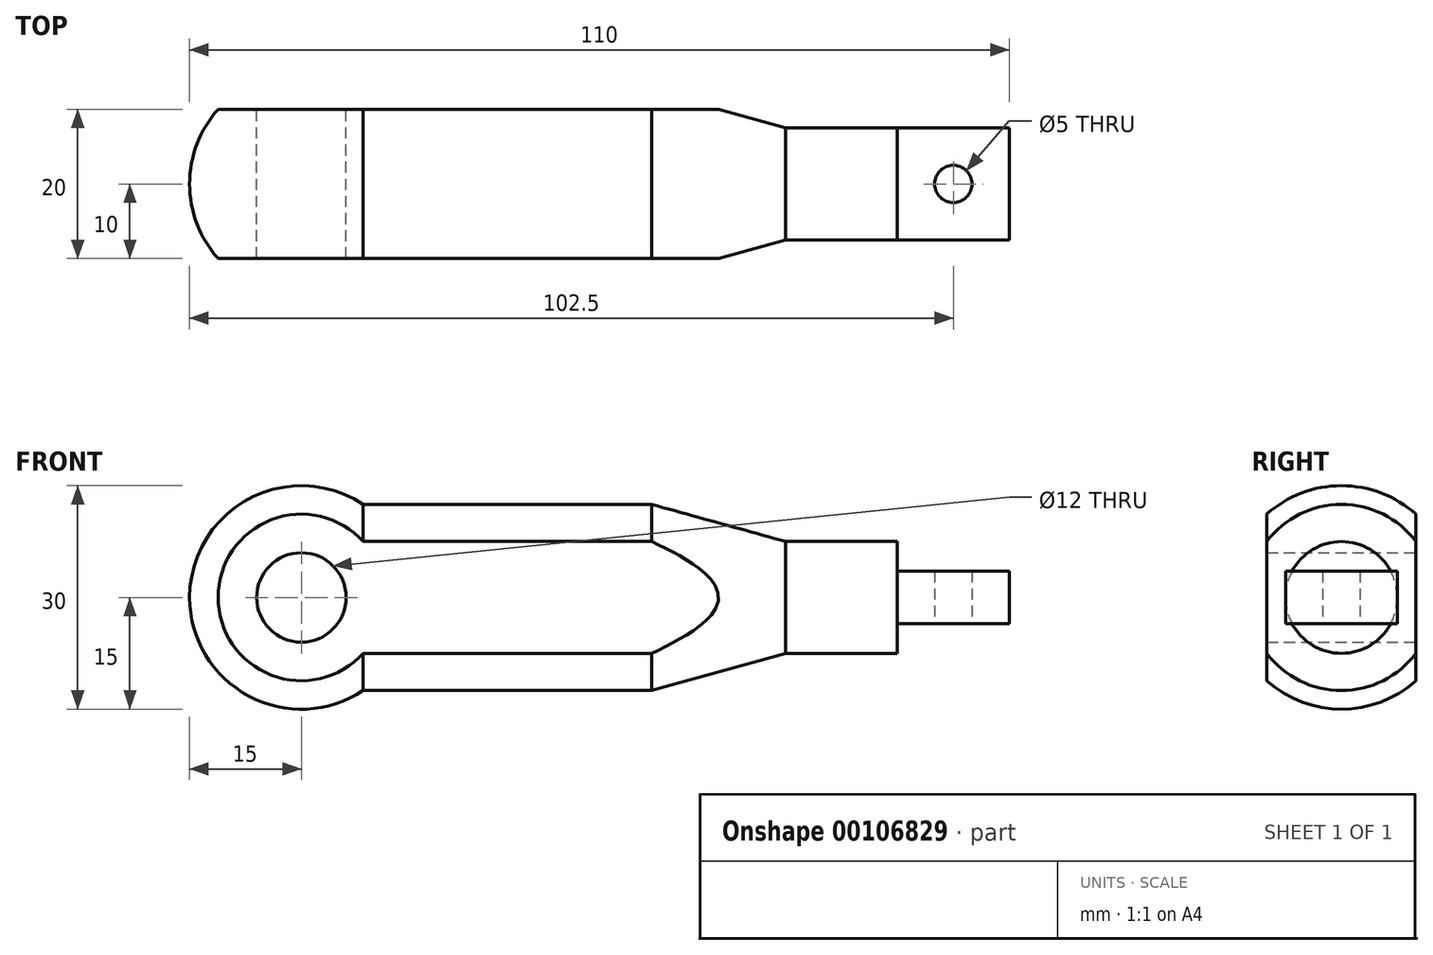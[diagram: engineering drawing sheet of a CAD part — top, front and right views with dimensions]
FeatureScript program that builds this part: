
annotation { "Feature Type Name" : "Feature", "Feature Type Description" : "" }
export const myFeature = defineFeature(function(context is Context, id is Id, definition is map)
    precondition{}
    {
        {
            var Q0;
            Q0=qCreatedBy(makeId("Front.planeOp"),FACE);
            var sketch = newSketch(context, id + "F0", { "sketchPlane" : qUnion([Q0])});
            skCircle(sketch, "E0", {"center": v(0, 0) * mm, "radius": 6 * mm});
            skLineSegment(sketch, "E1", {"start": v(0, 0) * mm, "end": v(135.17, 0) * mm, "construction": true});
            skLineSegment(sketch, "E2.bottom", {"start": v(80, 3.5) * mm, "end": v(95, 3.5) * mm});
            skLineSegment(sketch, "E2.top", {"start": v(80, -3.5) * mm, "end": v(95, -3.5) * mm});
            skLineSegment(sketch, "E2.left", {"start": v(80, 3.5) * mm, "end": v(80, -3.5) * mm});
            skLineSegment(sketch, "E2.right", {"start": v(95, 3.5) * mm, "end": v(95, -3.5) * mm});
            skSolve(sketch);
        }
        {
            var Q0;
            Q0=makeQuery(id+"F0.imprint","IMPRINT",FACE,{"disambiguationData":[TD([[makeQuery(id+"F0.imprint","IMPRINT",EDGE,{"derivedFrom":sQuery(id+"F0.wireOp",EDGE,"E2.bottom")}),-1.0]])]});
            extrude(context, id + "F1", {"entities" : qUnion([Q0]), "endBound" : BoundingType.SYMMETRIC, "depth" : 15 * mm});
        }
        {
            var Q0;
            Q0=qCreatedBy(makeId("Top.planeOp"),FACE);
            var sketch = newSketch(context, id + "F2", { "sketchPlane" : qUnion([Q0])});
            skLineSegment(sketch, "E3", {"start": v(-1.5, 0) * mm, "end": v(118.55, 0) * mm, "construction": true});
            skCircle(sketch, "E4", {"center": v(87.5, 0) * mm, "radius": 2.5 * mm});
            skSolve(sketch);
        }
        {
            var Q0;
            Q0=qCreatedBy(makeId("Front.planeOp"),FACE);
            var sketch = newSketch(context, id + "F3", { "sketchPlane" : qUnion([Q0])});
            skLineSegment(sketch, "E5.bottom", {"start": v(65, 7.5) * mm, "end": v(80, 7.5) * mm});
            skLineSegment(sketch, "E5.top", {"start": v(65, 0) * mm, "end": v(80, 0) * mm});
            skLineSegment(sketch, "E5.left", {"start": v(65, 7.5) * mm, "end": v(65, 0) * mm});
            skLineSegment(sketch, "E5.right", {"start": v(80, 7.5) * mm, "end": v(80, 0) * mm});
            skSolve(sketch);
        }
        {
            var Q0;
            Q0=makeQuery(id+"F3.imprint","IMPRINT",FACE,{"disambiguationData":[TD([[makeQuery(id+"F3.imprint","IMPRINT",EDGE,{"derivedFrom":sQuery(id+"F3.wireOp",EDGE,"E5.bottom")}),-1.0]])]});
            var Q1;
            Q1=sQuery(id+"F2.wireOp",EDGE,"E3");
            revolve(context, id + "F4", {"operationType" : NewBodyOperationType.ADD, "entities" : qUnion([Q0]), "axis" : qUnion([Q1]), "revolveType" : RevolveType.FULL});
        }
        {
            var Q0;
            Q0=qCreatedBy(makeId("Front.planeOp"),FACE);
            var sketch = newSketch(context, id + "F5", { "sketchPlane" : qUnion([Q0])});
            skLineSegment(sketch, "E6", {"start": v(8.3, 12.5) * mm, "end": v(47, 12.5) * mm});
            skLineSegment(sketch, "E7", {"start": v(47, 12.5) * mm, "end": v(65, 7.5) * mm});
            skArc(sketch, "E8", {"start": v(8.3, 12.5) * mm, "mid": v(-7.1, 13.22) * mm, "end": v(-15, 0) * mm});
            skLineSegment(sketch, "E9", {"start": v(-15, 0) * mm, "end": v(65, 0) * mm});
            skLineSegment(sketch, "E10", {"start": v(65, 7.5) * mm, "end": v(65, 0) * mm});
            skSolve(sketch);
        }
        {
            var Q0;
            Q0=makeQuery(id+"F5.imprint","IMPRINT",FACE,{"disambiguationData":[TD([[makeQuery(id+"F5.imprint","IMPRINT",EDGE,{"derivedFrom":sQuery(id+"F5.wireOp",EDGE,"E6")}),-1.0]])]});
            var Q1;
            Q1=sQuery(id+"F5.wireOp",EDGE,"E9");
            revolve(context, id + "F6", {"operationType" : NewBodyOperationType.ADD, "entities" : qUnion([Q0]), "axis" : qUnion([Q1]), "revolveType" : RevolveType.FULL});
        }
        {
            var Q0;
            Q0=makeQuery(id+"F0.imprint","IMPRINT",FACE,{"disambiguationData":[TD([[makeQuery(id+"F0.imprint","IMPRINT",EDGE,{"derivedFrom":sQuery(id+"F0.wireOp",EDGE,"E0")}),1.0]])]});
            extrude(context, id + "F7", {"entities" : qUnion([Q0]), "operationType" : NewBodyOperationType.REMOVE, "endBound" : BoundingType.SYMMETRIC, "depth" : 30 * mm});
        }
        {
            var Q0;
            Q0=qCreatedBy(makeId("Top.planeOp"),FACE);
            var sketch = newSketch(context, id + "F8", { "sketchPlane" : qUnion([Q0])});
            skCircle(sketch, "E11", {"center": v(87.5, 0) * mm, "radius": 2.5 * mm});
            skSolve(sketch);
        }
        {
            var Q0;
            Q0=makeQuery(id+"F8.imprint","IMPRINT",FACE,{"disambiguationData":[TD([[makeQuery(id+"F8.imprint","IMPRINT",EDGE,{"derivedFrom":sQuery(id+"F8.wireOp",EDGE,"E11")}),1.0]])]});
            var Q1;
            Q1=sQuery(id+"F8.wireOp",EDGE,"E11");
            extrude(context, id + "F9", {"entities" : qUnion([Q0]), "operationType" : NewBodyOperationType.REMOVE, "surfaceEntities" : qUnion([Q1]), "endBound" : BoundingType.SYMMETRIC, "depth" : 7 * mm});
        }
        {
            var Q0;
            Q0=qCreatedBy(makeId("Right.planeOp"),FACE);
            var sketch = newSketch(context, id + "F10", { "sketchPlane" : qUnion([Q0])});
            skLineSegment(sketch, "E12.bottom", {"start": v(-15, 15) * mm, "end": v(-10, 15) * mm});
            skLineSegment(sketch, "E12.top", {"start": v(-15, -15) * mm, "end": v(-10, -15) * mm});
            skLineSegment(sketch, "E12.left", {"start": v(-15, 15) * mm, "end": v(-15, -15) * mm});
            skLineSegment(sketch, "E12.right", {"start": v(-10, 15) * mm, "end": v(-10, -15) * mm});
            skLineSegment(sketch, "E13.bottom", {"start": v(10, 15) * mm, "end": v(15, 15) * mm});
            skLineSegment(sketch, "E13.top", {"start": v(10, -15) * mm, "end": v(15, -15) * mm});
            skLineSegment(sketch, "E13.left", {"start": v(10, 15) * mm, "end": v(10, -15) * mm});
            skLineSegment(sketch, "E13.right", {"start": v(15, 15) * mm, "end": v(15, -15) * mm});
            skLineSegment(sketch, "E14", {"start": v(-20.85, 0) * mm, "end": v(24.09, 0) * mm, "construction": true});
            skSolve(sketch);
        }
        {
            var Q0;
            Q0=makeQuery(id+"F10.imprint","IMPRINT",FACE,{"disambiguationData":[TD([[makeQuery(id+"F10.imprint","IMPRINT",EDGE,{"derivedFrom":sQuery(id+"F10.wireOp",EDGE,"E13.bottom")}),-1.0]])]});
            extrude(context, id + "F11", {"entities" : qUnion([Q0]), "operationType" : NewBodyOperationType.REMOVE, "endBound" : BoundingType.SYMMETRIC, "depth" : 150 * mm});
        }
        {
            var Q0;
            Q0=makeQuery(id+"F10.imprint","IMPRINT",FACE,{"disambiguationData":[TD([[makeQuery(id+"F10.imprint","IMPRINT",EDGE,{"derivedFrom":sQuery(id+"F10.wireOp",EDGE,"E12.bottom")}),-1.0]])]});
            extrude(context, id + "F12", {"entities" : qUnion([Q0]), "operationType" : NewBodyOperationType.REMOVE, "endBound" : BoundingType.SYMMETRIC, "oppositeDirection" : true, "depth" : 150 * mm});
        }
    });
